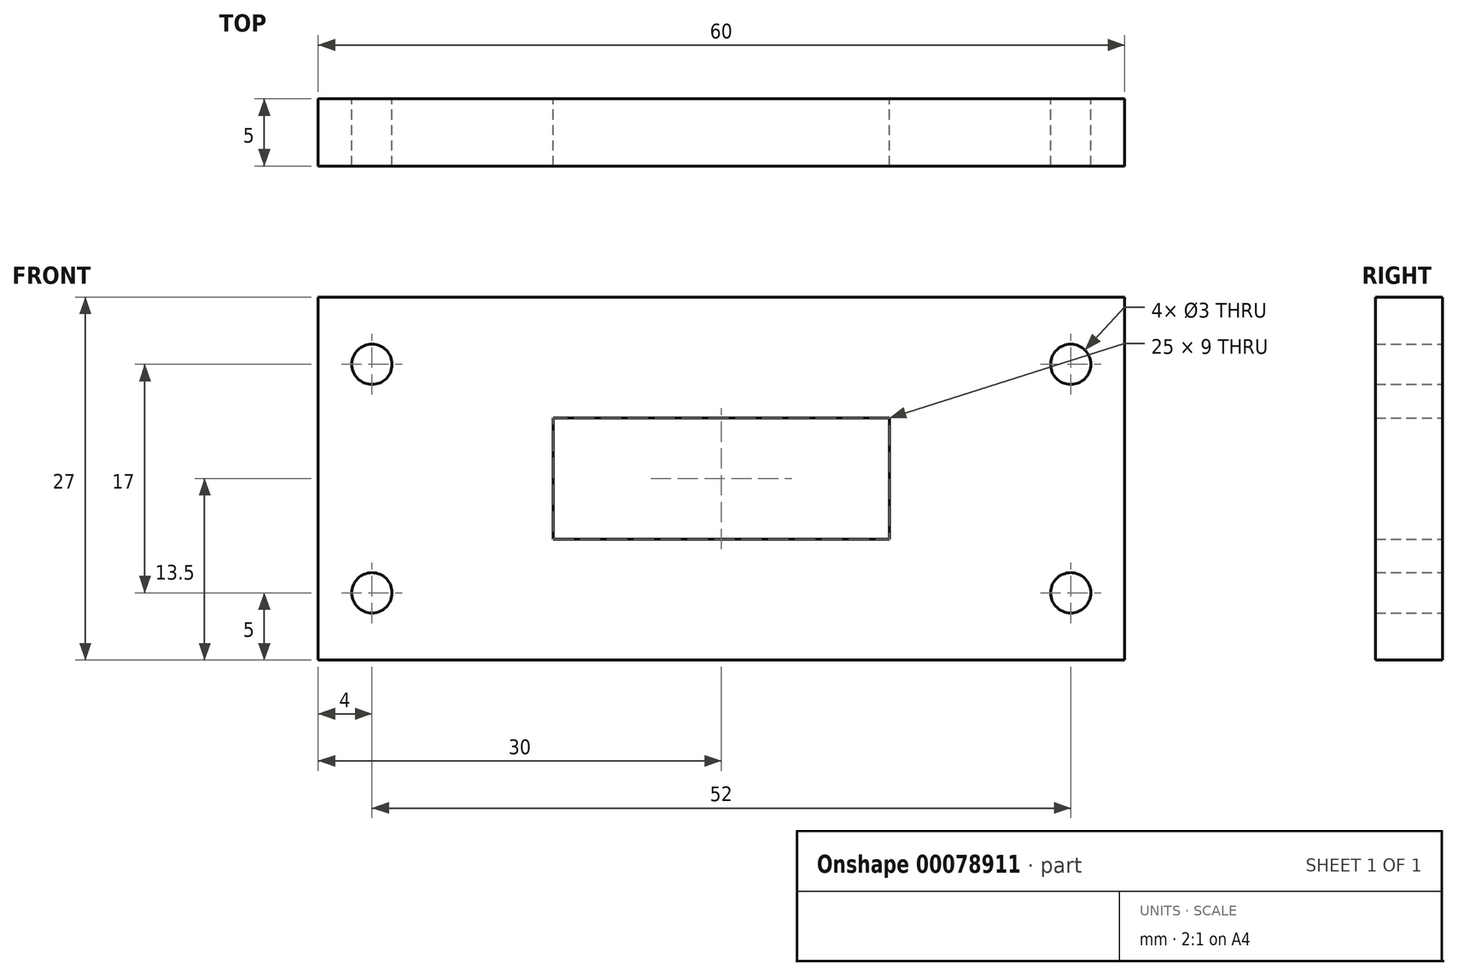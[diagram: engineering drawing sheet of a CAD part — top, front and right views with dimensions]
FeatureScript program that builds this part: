
annotation { "Feature Type Name" : "Feature", "Feature Type Description" : "" }
export const myFeature = defineFeature(function(context is Context, id is Id, definition is map)
    precondition{}
    {
        {
            var Q0;
            Q0=qCreatedBy(makeId("Front.planeOp"),FACE);
            var sketch = newSketch(context, id + "F0", { "sketchPlane" : qUnion([Q0])});
            skLineSegment(sketch, "E0.bottom", {"start": v(0, 0) * mm, "end": v(60, 0) * mm});
            skLineSegment(sketch, "E0.top", {"start": v(0, 27) * mm, "end": v(60, 27) * mm});
            skLineSegment(sketch, "E0.left", {"start": v(0, 0) * mm, "end": v(0, 27) * mm});
            skLineSegment(sketch, "E0.right", {"start": v(60, 0) * mm, "end": v(60, 27) * mm});
            skLineSegment(sketch, "E1", {"start": v(30, 27) * mm, "end": v(30, 0) * mm, "construction": true});
            skLineSegment(sketch, "E2", {"start": v(0, 13.5) * mm, "end": v(60, 13.5) * mm, "construction": true});
            skCircle(sketch, "E3", {"center": v(4, 22) * mm, "radius": 1.5 * mm});
            skCircle(sketch, "E4.MirrorC", {"center": v(56, 22) * mm, "radius": 1.5 * mm});
            skCircle(sketch, "E5.MirrorC", {"center": v(4, 5) * mm, "radius": 1.5 * mm});
            skCircle(sketch, "E6.MirrorC", {"center": v(56, 5) * mm, "radius": 1.5 * mm});
            skLineSegment(sketch, "E7", {"start": v(30, 18) * mm, "end": v(17.5, 18) * mm});
            skLineSegment(sketch, "E8", {"start": v(17.5, 18) * mm, "end": v(17.5, 13.5) * mm});
            skLineSegment(sketch, "E9.MirrorCS", {"start": v(30, 18) * mm, "end": v(42.5, 18) * mm});
            skLineSegment(sketch, "E10.MirrorCS", {"start": v(42.5, 18) * mm, "end": v(42.5, 13.5) * mm});
            skLineSegment(sketch, "E11.MirrorCS", {"start": v(17.5, 9) * mm, "end": v(17.5, 13.5) * mm});
            skLineSegment(sketch, "E12.MirrorCS", {"start": v(30, 9) * mm, "end": v(17.5, 9) * mm});
            skLineSegment(sketch, "E13.MirrorCS", {"start": v(30, 9) * mm, "end": v(42.5, 9) * mm});
            skLineSegment(sketch, "E14.MirrorCS", {"start": v(42.5, 9) * mm, "end": v(42.5, 13.5) * mm});
            skSolve(sketch);
        }
        {
            var Q0;
            Q0=makeQuery(id+"F0.imprint","IMPRINT",FACE,{"disambiguationData":[TD([[makeQuery(id+"F0.imprint","IMPRINT",EDGE,{"derivedFrom":sQuery(id+"F0.wireOp",EDGE,"E0.bottom")}),1.0]])]});
            extrude(context, id + "F1", {"entities" : qUnion([Q0]), "depth" : 5 * mm});
        }
    });
